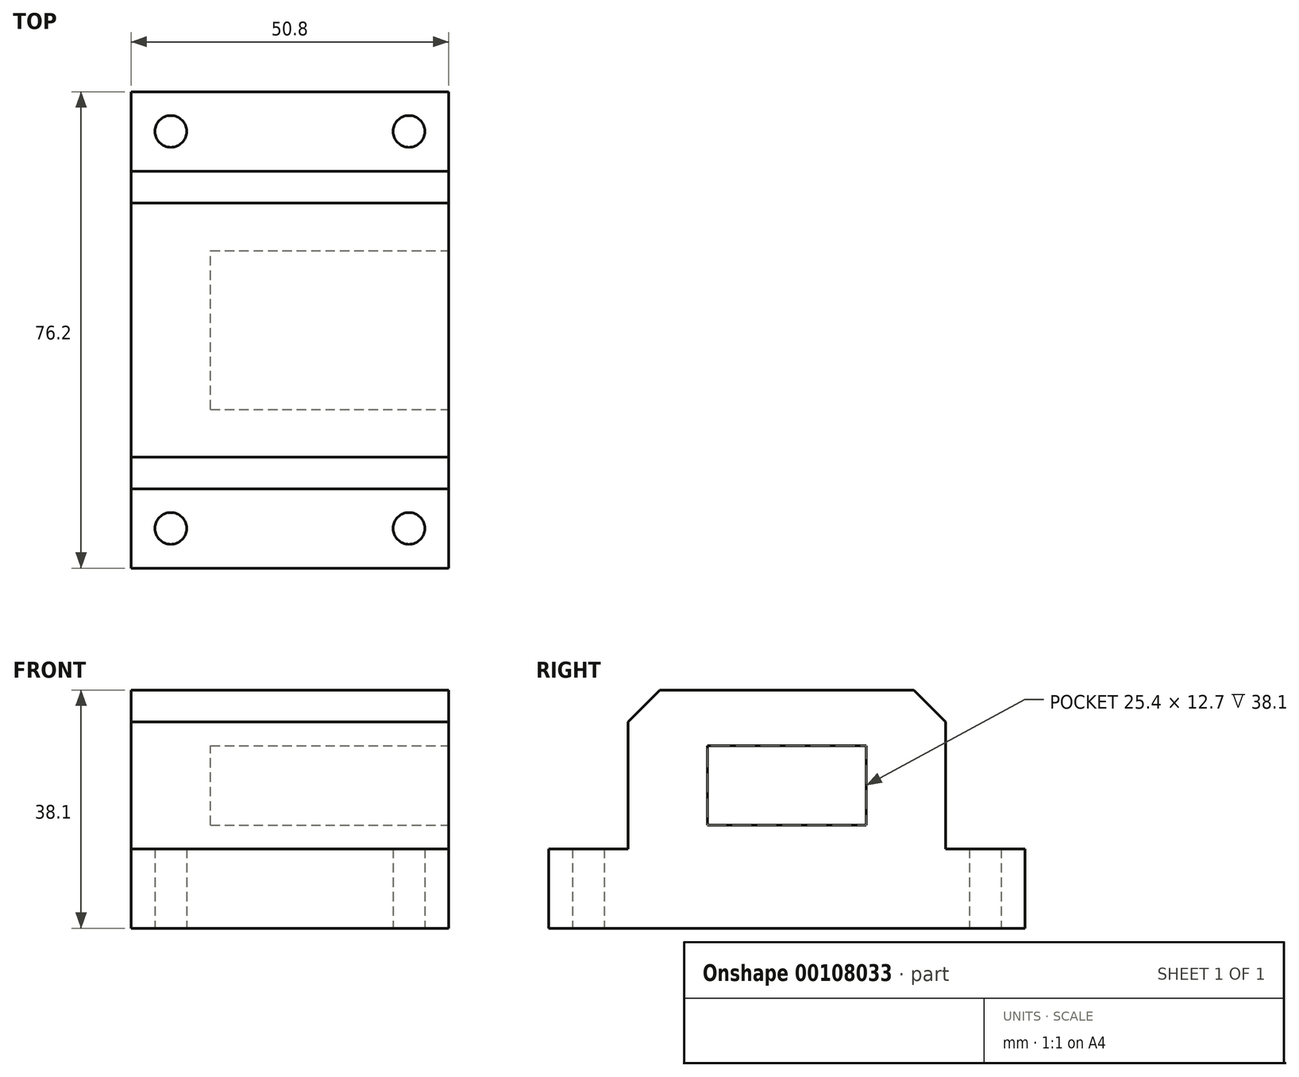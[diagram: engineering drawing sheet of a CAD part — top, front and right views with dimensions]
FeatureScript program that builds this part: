
annotation { "Feature Type Name" : "Feature", "Feature Type Description" : "" }
export const myFeature = defineFeature(function(context is Context, id is Id, definition is map)
    precondition{}
    {
        {
            var Q0;
            Q0=qCreatedBy(makeId("Top.planeOp"),FACE);
            var sketch = newSketch(context, id + "F0", { "sketchPlane" : qUnion([Q0])});
            skLineSegment(sketch, "E0.bottom", {"start": v(-101.6, 50.8) * mm, "end": v(-50.8, 50.8) * mm});
            skLineSegment(sketch, "E0.top", {"start": v(-101.6, -25.4) * mm, "end": v(-50.8, -25.4) * mm});
            skLineSegment(sketch, "E0.left", {"start": v(-101.6, 50.8) * mm, "end": v(-101.6, -25.4) * mm});
            skLineSegment(sketch, "E0.right", {"start": v(-50.8, 50.8) * mm, "end": v(-50.8, -25.4) * mm});
            skLineSegment(sketch, "E1", {"start": v(-101.6, 38.1) * mm, "end": v(-50.8, 38.1) * mm});
            skLineSegment(sketch, "E2", {"start": v(-101.6, -12.7) * mm, "end": v(-50.8, -12.7) * mm});
            skCircle(sketch, "E3", {"center": v(-95.25, 44.45) * mm, "radius": 2.54 * mm});
            skCircle(sketch, "E4", {"center": v(-57.15, 44.45) * mm, "radius": 2.54 * mm});
            skCircle(sketch, "E5", {"center": v(-57.15, -19.05) * mm, "radius": 2.54 * mm});
            skCircle(sketch, "E6", {"center": v(-95.25, -19.05) * mm, "radius": 2.54 * mm});
            skLineSegment(sketch, "E7", {"start": v(-101.6, 44.45) * mm, "end": v(-50.8, 44.45) * mm, "construction": true});
            skLineSegment(sketch, "E8", {"start": v(-101.6, -19.05) * mm, "end": v(-50.8, -19.05) * mm, "construction": true});
            skLineSegment(sketch, "E9", {"start": v(-50.8, -12.7) * mm, "end": v(-101.6, 38.1) * mm, "construction": true});
            skPoint(sketch, "E10", {"position": v(-76.2, 12.7) * mm});
            skSolve(sketch);
        }
        {
            var Q0;
            {var subQ0=sQuery(id+"F0.wireOp",EDGE,"E1");Q0=makeQuery(id+"F0.imprint","IMPRINT",FACE,{"disambiguationData":[TD([[makeQuery(id+"F0.imprint","IMPRINT",EDGE,{"derivedFrom":subQ0}),-1.0]])]});}
            extrude(context, id + "F1", {"entities" : qUnion([Q0]), "depth" : 38.1 * mm});
        }
        {
            var Q0;
            {var subQ2=sQuery(id+"F0.wireOp",EDGE,"E0.top");Q0=makeQuery(id+"F0.imprint","IMPRINT",FACE,{"disambiguationData":[TD([[makeQuery(id+"F0.imprint","IMPRINT",EDGE,{"derivedFrom":subQ2}),1.0]])]});}
            var Q1;
            {var subQ2=sQuery(id+"F0.wireOp",EDGE,"E0.bottom");Q1=makeQuery(id+"F0.imprint","IMPRINT",FACE,{"disambiguationData":[TD([[makeQuery(id+"F0.imprint","IMPRINT",EDGE,{"derivedFrom":subQ2}),-1.0]])]});}
            extrude(context, id + "F2", {"entities" : qUnion([Q0, Q1]), "operationType" : NewBodyOperationType.ADD, "depth" : 12.7 * mm});
        }
        {
            var Q0;
            Q0=makeQuery(id+"F1.opExtrude","CAP_EDGE",EDGE,{"disambiguationData":[OSD([sQuery(id+"F0.wireOp",EDGE,"E1")])],"isStart":false});
            var Q1;
            Q1=makeQuery(id+"F1.opExtrude","CAP_EDGE",EDGE,{"disambiguationData":[OSD([sQuery(id+"F0.wireOp",EDGE,"E2")])],"isStart":false});
            chamfer(context, id + "F3", {"entities" : qUnion([Q0, Q1]), "width" : 5.08 * mm, "tangentPropagation" : true});
        }
        {
            var Q0;
            {var subQ0=sQuery(id+"F0.wireOp",EDGE,"E0.right");Q0=makeQuery(id+"F2.boolean.opBoolean","MERGE",FACE,{"derivedFrom":[makeQuery(id+"F1.opExtrude","SWEPT_FACE",FACE,{"disambiguationData":[OSD([subQ0])]}),makeQuery(id+"F2.opExtrude","SWEPT_FACE",FACE,{"disambiguationData":[OSD([subQ0]),TDD([makeQuery(id+"F0.imprint","IMPRINT",EDGE,{"disambiguationData":[TD([[makeQuery(id+"F0.imprint","INTERSECT",VERTEX,{"derivedFrom":[sQuery(id+"F0.wireOp",EDGE,"E0.bottom"),subQ0]}),-1.0]])],"derivedFrom":subQ0})])]}),makeQuery(id+"F2.opExtrude","SWEPT_FACE",FACE,{"disambiguationData":[OSD([subQ0]),TDD([makeQuery(id+"F0.imprint","IMPRINT",EDGE,{"disambiguationData":[TD([[makeQuery(id+"F0.imprint","INTERSECT",VERTEX,{"derivedFrom":[sQuery(id+"F0.wireOp",EDGE,"E0.top"),subQ0]}),1.0]])],"derivedFrom":subQ0})])]})]});}
            var sketch = newSketch(context, id + "F4", { "sketchPlane" : qUnion([Q0])});
            skLineSegment(sketch, "E11.bottom", {"start": v(0, 16.5) * mm, "end": v(25.4, 16.51) * mm});
            skLineSegment(sketch, "E11.top", {"start": v(0, 29.21) * mm, "end": v(25.4, 29.21) * mm});
            skLineSegment(sketch, "E11.left", {"start": v(0, 16.5) * mm, "end": v(0, 29.21) * mm});
            skLineSegment(sketch, "E11.right", {"start": v(25.4, 16.51) * mm, "end": v(25.4, 29.21) * mm});
            skSolve(sketch);
        }
        {
            var Q0;
            Q0=makeQuery(id+"F4.imprint","IMPRINT",FACE,{"disambiguationData":[TD([[makeQuery(id+"F4.imprint","IMPRINT",EDGE,{"derivedFrom":sQuery(id+"F4.wireOp",EDGE,"E11.bottom")}),1.0]])]});
            extrude(context, id + "F5", {"entities" : qUnion([Q0]), "operationType" : NewBodyOperationType.REMOVE, "oppositeDirection" : true, "depth" : 38.1 * mm});
        }
    });
